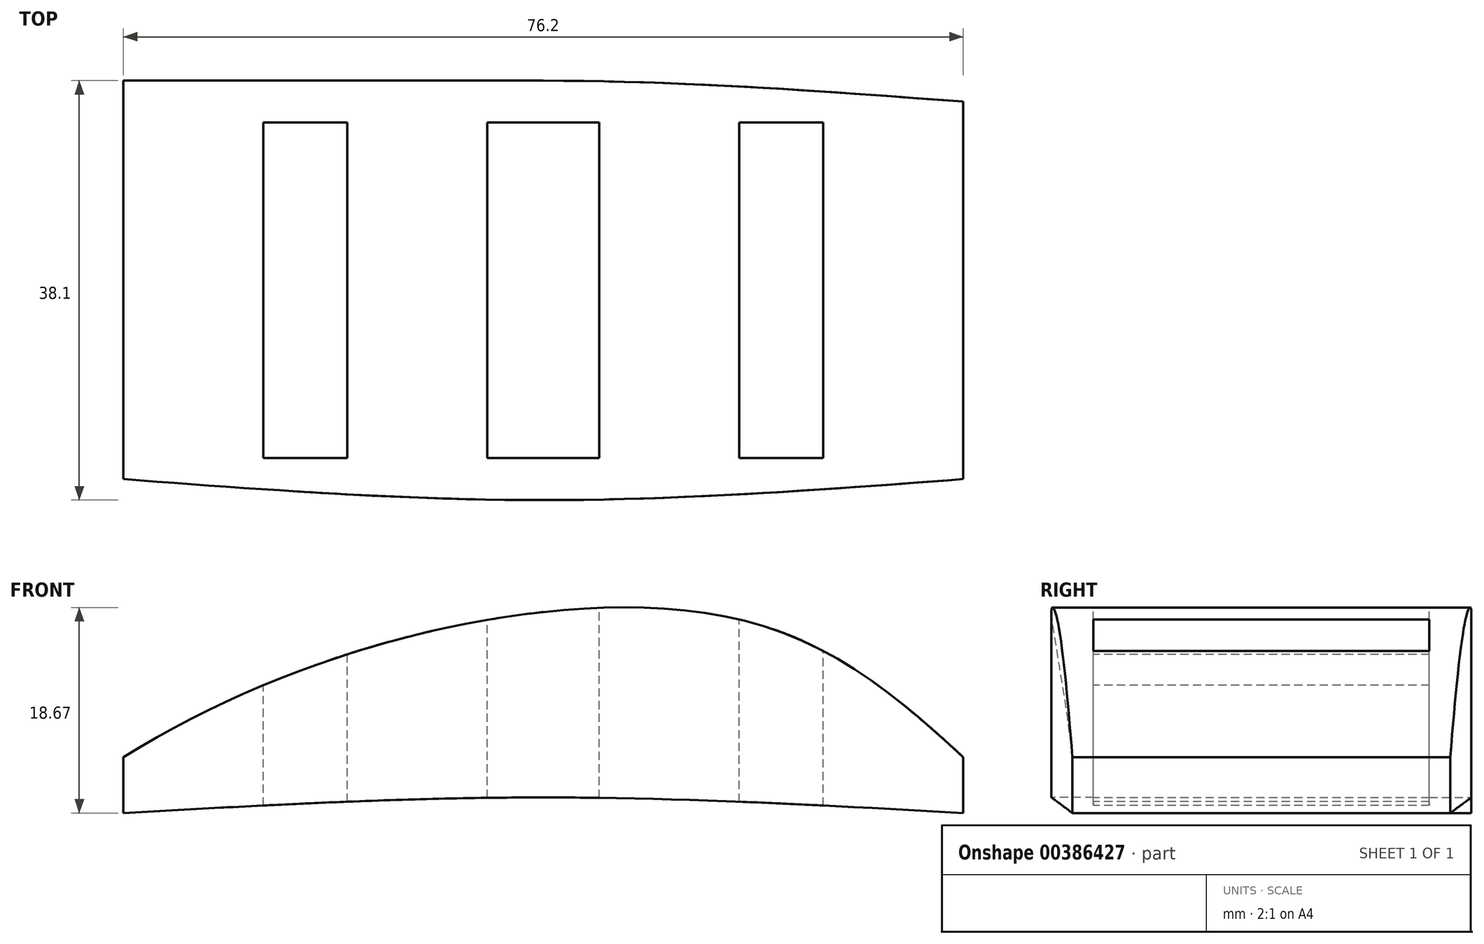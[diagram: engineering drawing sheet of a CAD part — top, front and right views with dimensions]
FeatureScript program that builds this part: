
annotation { "Feature Type Name" : "Feature", "Feature Type Description" : "" }
export const myFeature = defineFeature(function(context is Context, id is Id, definition is map)
    precondition{}
    {
        {
            var Q0;
            Q0=qCreatedBy(makeId("Top.planeOp"),FACE);
            var sketch = newSketch(context, id + "F0", { "sketchPlane" : qUnion([Q0])});
            skLineSegment(sketch, "E0.bottom", {"start": v(0, 0) * mm, "end": v(76.2, 0) * mm});
            skLineSegment(sketch, "E0.top", {"start": v(0, -38.1) * mm, "end": v(76.2, -38.1) * mm});
            skLineSegment(sketch, "E0.left", {"start": v(0, 0) * mm, "end": v(0, -38.1) * mm});
            skLineSegment(sketch, "E0.right", {"start": v(76.2, 0) * mm, "end": v(76.2, -38.1) * mm});
            skSolve(sketch);
        }
        {
            var Q0;
            Q0 = qSketchRegion(id + "F0", true);
            extrude(context, id + "F1", {"entities" : qUnion([Q0]), "depth" : 27.94 * mm});
        }
        {
            var Q0;
            Q0=makeQuery(id+"F1.opExtrude","SWEPT_FACE",FACE,{"disambiguationData":[OSD([sQuery(id+"F0.wireOp",EDGE,"E0.top")])]});
            cPlane(context, id + "F2", {"entities" : qUnion([Q0]), "cplaneType" : CPlaneType.OFFSET, "offset" : 0 * mm, "width" : 152.4 * mm, "height" : 152.4 * mm});
        }
        {
            var Q0;
            Q0=qCreatedBy(id+"F2.planeOp",FACE);
            var sketch = newSketch(context, id + "F3", { "sketchPlane" : qUnion([Q0])});
            skLineSegment(sketch, "E1", {"start": v(0, 0) * mm, "end": v(38.1, 0) * mm});
            skLineSegment(sketch, "E2", {"start": v(38.1, 0) * mm, "end": v(76.2, 0) * mm});
            skFitSpline(sketch, "E3", {"points": [v(0, 0) * mm, v(38.1, 1.42) * mm, v(76.2, 0) * mm], "startDerivative": vector(76.2, 4.25) * mm, "endDerivative": vector(76.2, -4.25) * mm});
            skLineSegment(sketch, "E4", {"start": v(0, 0) * mm, "end": v(0, 5.08) * mm});
            skFitSpline(sketch, "E5", {"points": [v(0, 5.08) * mm, v(51.06, 18.4) * mm, v(76.2, 5.08) * mm], "startDerivative": vector(88.98, 55.28) * mm, "endDerivative": vector(62.75, -58.18) * mm});
            skLineSegment(sketch, "E6", {"start": v(76.2, 5.08) * mm, "end": v(76.2, 0) * mm});
            skSolve(sketch);
        }
        {
            var Q0;
            Q0=makeQuery(id+"F1.opExtrude","SWEPT_FACE",FACE,{"disambiguationData":[OSD([sQuery(id+"F0.wireOp",EDGE,"E0.top")])]});
            extrude(context, id + "F4", {"entities" : qUnion([Q0]), "operationType" : NewBodyOperationType.REMOVE, "oppositeDirection" : true, "depth" : 38.1 * mm});
        }
        {
            var Q0;
            Q0=makeQuery(id+"F3.imprint","IMPRINT",FACE,{"disambiguationData":[TD([[makeQuery(id+"F3.imprint","IMPRINT",EDGE,{"derivedFrom":sQuery(id+"F3.wireOp",EDGE,"E3")}),1.0]])]});
            extrude(context, id + "F5", {"entities" : qUnion([Q0]), "oppositeDirection" : true, "depth" : 38.1 * mm});
        }
        {
            var Q0;
            Q0=qCreatedBy(makeId("Top.planeOp"),FACE);
            cPlane(context, id + "F6", {"entities" : qUnion([Q0]), "cplaneType" : CPlaneType.OFFSET, "offset" : 25.4 * mm, "width" : 152.4 * mm, "height" : 152.4 * mm});
        }
        {
            var Q0;
            Q0=qCreatedBy(id+"F6.planeOp",FACE);
            var sketch = newSketch(context, id + "F7", { "sketchPlane" : qUnion([Q0])});
            skLineSegment(sketch, "E7", {"start": v(0, 0) * mm, "end": v(0, -19.05) * mm});
            skLineSegment(sketch, "E8", {"start": v(0, -19.05) * mm, "end": v(38.1, -19.05) * mm});
            skLineSegment(sketch, "E9", {"start": v(38.1, -19.05) * mm, "end": v(76.2, -19.05) * mm});
            skLineSegment(sketch, "E10", {"start": v(38.1, -19.05) * mm, "end": v(38.1, -34.3) * mm});
            skLineSegment(sketch, "E11", {"start": v(38.1, -19.05) * mm, "end": v(38.1, -3.8) * mm});
            skLineSegment(sketch, "E12", {"start": v(38.1, -34.3) * mm, "end": v(0, -34.3) * mm});
            skLineSegment(sketch, "E13", {"start": v(38.1, -34.3) * mm, "end": v(76.2, -34.3) * mm});
            skLineSegment(sketch, "E14", {"start": v(38.1, -3.8) * mm, "end": v(0, -3.8) * mm});
            skLineSegment(sketch, "E15", {"start": v(38.1, -3.8) * mm, "end": v(76.2, -3.8) * mm});
            skLineSegment(sketch, "E16", {"start": v(0, -34.3) * mm, "end": v(0, -36.2) * mm});
            skLineSegment(sketch, "E17", {"start": v(0, -3.8) * mm, "end": v(0, -1.9) * mm});
            skLineSegment(sketch, "E18", {"start": v(76.2, -3.8) * mm, "end": v(76.2, -1.9) * mm});
            skLineSegment(sketch, "E19", {"start": v(76.2, -34.3) * mm, "end": v(76.2, -36.2) * mm});
            skLineSegment(sketch, "E20", {"start": v(38.1, -34.3) * mm, "end": v(38.1, -38.1) * mm});
            skFitSpline(sketch, "E21", {"points": [v(0, -36.2) * mm, v(38.1, -38.1) * mm, v(76.2, -36.2) * mm], "startDerivative": vector(76.2, -5.71) * mm, "endDerivative": vector(76.2, 5.72) * mm});
            skLineSegment(sketch, "E22", {"start": v(38.1, -3.8) * mm, "end": v(38.1, 0) * mm});
            skFitSpline(sketch, "E23", {"points": [v(0, -1.9) * mm, v(38.1, 0) * mm, v(76.2, -1.9) * mm], "startDerivative": vector(76.2, 5.72) * mm, "endDerivative": vector(76.2, -5.71) * mm});
            skLineSegment(sketch, "E24", {"start": v(0, -36.2) * mm, "end": v(0, -38.1) * mm});
            skLineSegment(sketch, "E25", {"start": v(0, -38.1) * mm, "end": v(76.2, -38.1) * mm});
            skLineSegment(sketch, "E26", {"start": v(76.2, -38.1) * mm, "end": v(76.2, -36.2) * mm});
            skLineSegment(sketch, "E27", {"start": v(0, -1.9) * mm, "end": v(0, 0) * mm});
            skLineSegment(sketch, "E28", {"start": v(0, 0) * mm, "end": v(76.2, 0) * mm});
            skLineSegment(sketch, "E29", {"start": v(76.2, 0) * mm, "end": v(76.2, -1.9) * mm});
            skSolve(sketch);
        }
        {
            var Q0;
            {var subQ0=sQuery(id+"F7.wireOp",EDGE,"E24");Q0=makeQuery(id+"F7.imprint","IMPRINT",FACE,{"disambiguationData":[TD([[makeQuery(id+"F7.imprint","IMPRINT",EDGE,{"derivedFrom":subQ0}),1.0]])]});}
            var Q1;
            {var subQ0=sQuery(id+"F7.wireOp",EDGE,"E26");Q1=makeQuery(id+"F7.imprint","IMPRINT",FACE,{"disambiguationData":[TD([[makeQuery(id+"F7.imprint","IMPRINT",EDGE,{"derivedFrom":subQ0}),1.0]])]});}
            var Q2;
            {var subQ0=sQuery(id+"F7.wireOp",EDGE,"E29");Q2=makeQuery(id+"F7.imprint","IMPRINT",FACE,{"disambiguationData":[TD([[makeQuery(id+"F7.imprint","IMPRINT",EDGE,{"derivedFrom":subQ0}),-1.0]])]});}
            var Q3;
            {var subQ0=sQuery(id+"F7.wireOp",EDGE,"E27");Q3=makeQuery(id+"F7.imprint","IMPRINT",FACE,{"disambiguationData":[TD([[makeQuery(id+"F7.imprint","IMPRINT",EDGE,{"derivedFrom":subQ0}),-1.0]])]});}
            extrude(context, id + "F8", {"entities" : qUnion([Q0, Q1, Q2, Q3]), "operationType" : NewBodyOperationType.REMOVE, "oppositeDirection" : true, "depth" : 30.73 * mm});
        }
        {
            var Q0;
            Q0=qCreatedBy(id+"F6.planeOp",FACE);
            var sketch = newSketch(context, id + "F9", { "sketchPlane" : qUnion([Q0])});
            skLineSegment(sketch, "E30", {"start": v(0, 0) * mm, "end": v(0, -19.05) * mm});
            skLineSegment(sketch, "E31", {"start": v(0, -19.05) * mm, "end": v(76.2, -19.05) * mm});
            skLineSegment(sketch, "E32", {"start": v(76.2, -19.05) * mm, "end": v(63.5, -19.05) * mm});
            skLineSegment(sketch, "E33", {"start": v(63.5, -19.05) * mm, "end": v(63.5, -3.8) * mm});
            skLineSegment(sketch, "E34", {"start": v(63.5, -19.05) * mm, "end": v(63.5, -34.29) * mm});
            skLineSegment(sketch, "E35", {"start": v(63.5, -3.8) * mm, "end": v(55.88, -3.8) * mm});
            skLineSegment(sketch, "E36", {"start": v(55.88, -3.8) * mm, "end": v(55.88, -19.05) * mm});
            skLineSegment(sketch, "E37", {"start": v(55.88, -19.05) * mm, "end": v(55.88, -34.29) * mm});
            skLineSegment(sketch, "E38", {"start": v(55.88, -34.29) * mm, "end": v(63.5, -34.29) * mm});
            skLineSegment(sketch, "E39", {"start": v(55.88, -19.05) * mm, "end": v(43.18, -19.05) * mm});
            skLineSegment(sketch, "E40", {"start": v(43.18, -19.05) * mm, "end": v(43.18, -3.8) * mm});
            skLineSegment(sketch, "E41", {"start": v(43.18, -19.05) * mm, "end": v(43.18, -34.29) * mm});
            skLineSegment(sketch, "E42", {"start": v(0, -19.05) * mm, "end": v(12.7, -19.05) * mm});
            skLineSegment(sketch, "E43", {"start": v(12.7, -19.05) * mm, "end": v(12.7, -3.8) * mm});
            skLineSegment(sketch, "E44", {"start": v(12.7, -19.05) * mm, "end": v(12.7, -34.29) * mm});
            skLineSegment(sketch, "E45", {"start": v(12.7, -3.8) * mm, "end": v(20.32, -3.8) * mm});
            skLineSegment(sketch, "E46", {"start": v(20.32, -3.8) * mm, "end": v(20.32, -34.3) * mm});
            skLineSegment(sketch, "E47", {"start": v(20.32, -34.3) * mm, "end": v(12.7, -34.3) * mm});
            skLineSegment(sketch, "E48", {"start": v(33.02, -3.8) * mm, "end": v(33.02, -34.3) * mm});
            skLineSegment(sketch, "E49", {"start": v(33.02, -3.8) * mm, "end": v(43.18, -3.8) * mm});
            skLineSegment(sketch, "E50", {"start": v(33.02, -34.3) * mm, "end": v(43.18, -34.3) * mm});
            skSolve(sketch);
        }
        {
            var Q0;
            Q0 = qSketchRegion(id + "F9", true);
            extrude(context, id + "F10", {"entities" : qUnion([Q0]), "operationType" : NewBodyOperationType.REMOVE, "oppositeDirection" : true, "depth" : 25.4 * mm});
        }
    });
